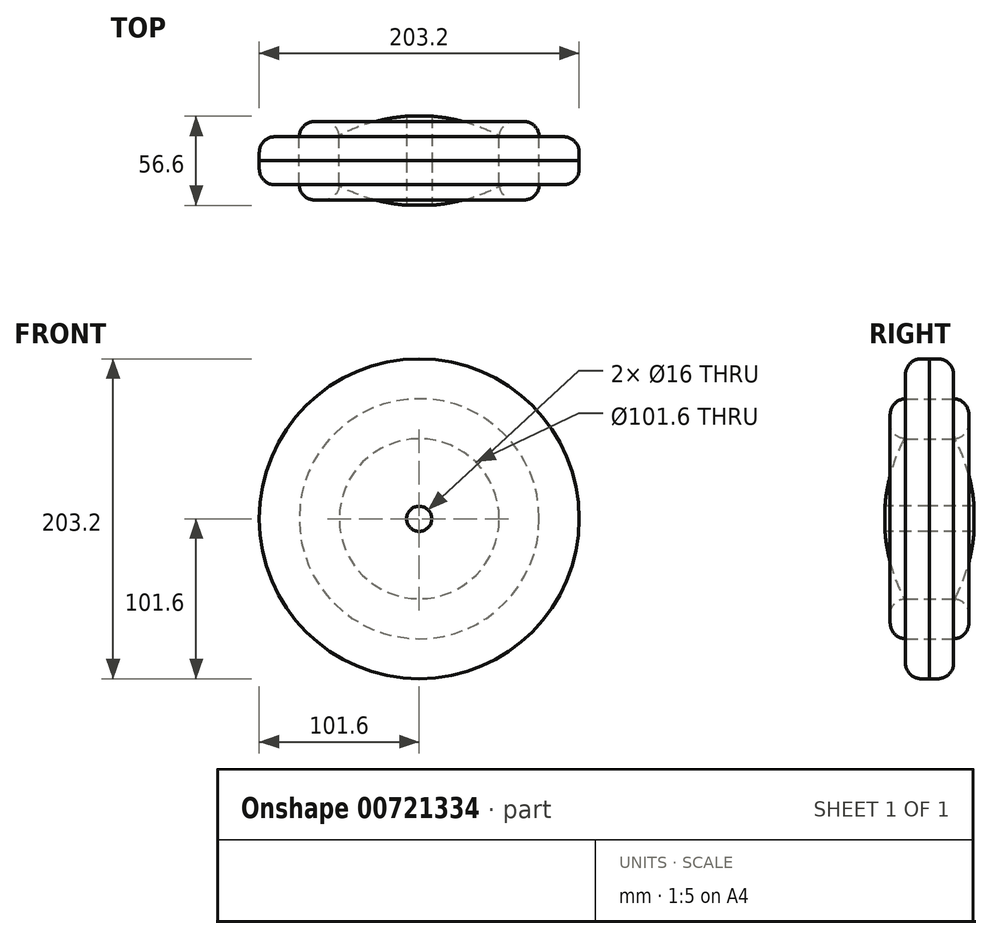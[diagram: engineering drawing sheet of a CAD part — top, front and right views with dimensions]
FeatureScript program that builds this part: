
annotation { "Feature Type Name" : "Feature", "Feature Type Description" : "" }
export const myFeature = defineFeature(function(context is Context, id is Id, definition is map)
    precondition{}
    {
        {
            var Q0;
            Q0=qCreatedBy(makeId("Front.planeOp"),FACE);
            var sketch = newSketch(context, id + "F0", { "sketchPlane" : qUnion([Q0])});
            skCircle(sketch, "E0", {"center": v(0, 0) * mm, "radius": 76.2 * mm});
            skCircle(sketch, "E1", {"center": v(0, 0) * mm, "radius": 50.8 * mm});
            skSolve(sketch);
        }
        {
            var Q0;
            Q0=makeQuery(id+"F0.imprint","IMPRINT",FACE,{"disambiguationData":[TD([[makeQuery(id+"F0.imprint","IMPRINT",EDGE,{"derivedFrom":sQuery(id+"F0.wireOp",EDGE,"E0")}),1.0]])]});
            extrude(context, id + "F1", {"entities" : qUnion([Q0]), "endBound" : BoundingType.SYMMETRIC, "depth" : 50 * mm, "offsetDistance" : 25 * mm});
        }
        {
            var Q0;
            Q0=makeQuery(id+"F1.opExtrude","CAP_EDGE",EDGE,{"disambiguationData":[OSD([sQuery(id+"F0.wireOp",EDGE,"E0")])],"isStart":false});
            var Q1;
            Q1=makeQuery(id+"F1.opExtrude","CAP_EDGE",EDGE,{"disambiguationData":[OSD([sQuery(id+"F0.wireOp",EDGE,"E0")])],"isStart":true});
            var Q2;
            Q2=makeQuery(id+"F1.opExtrude","CAP_EDGE",EDGE,{"disambiguationData":[OSD([sQuery(id+"F0.wireOp",EDGE,"E1")])],"isStart":false});
            var Q3;
            Q3=makeQuery(id+"F1.opExtrude","CAP_EDGE",EDGE,{"disambiguationData":[OSD([sQuery(id+"F0.wireOp",EDGE,"E1")])],"isStart":true});
            fillet(context, id + "F2", {"entities" : qUnion([Q0, Q1, Q2, Q3]), "radius" : 10 * mm, "tangentPropagation" : true, "allowEdgeOverflow" : false});
        }
        {
            var Q0;
            Q0=qCreatedBy(makeId("Right.planeOp"),FACE);
            var sketch = newSketch(context, id + "F3", { "sketchPlane" : qUnion([Q0])});
            skLineSegment(sketch, "E2", {"start": v(0, 0) * mm, "end": v(0, 101.6) * mm});
            skLineSegment(sketch, "E3", {"start": v(0, 101.6) * mm, "end": v(-5.28, 101.6) * mm});
            skLineSegment(sketch, "E4", {"start": v(-15.28, 91.6) * mm, "end": v(-15.28, 55.43) * mm});
            skLineSegment(sketch, "E5", {"start": v(0, 0) * mm, "end": v(-28.64, 0) * mm});
            skArc(sketch, "E6", {"start": v(-16.56, 50.04) * mm, "mid": v(-25.47, 25.72) * mm, "end": v(-28.64, 0) * mm});
            skPoint(sketch, "E7.visualSharp", {"position": v(-15.28, 52.5) * mm});
            skArc(sketch, "E7.filletArc", {"start": v(-16.56, 50.04) * mm, "mid": v(-15.6, 52.66) * mm, "end": v(-15.28, 55.43) * mm});
            skPoint(sketch, "E8.visualSharp", {"position": v(-15.28, 101.6) * mm});
            skArc(sketch, "E8.filletArc", {"start": v(-5.28, 101.6) * mm, "mid": v(-12.35, 98.67) * mm, "end": v(-15.28, 91.6) * mm});
            skSolve(sketch);
        }
        {
            var Q0;
            Q0 = qSketchRegion(id + "F3", true);
            var Q1;
            Q1=sQuery(id+"F3.wireOp",EDGE,"E5");
            revolve(context, id + "F4", {"surfaceOperationType" : NewSurfaceOperationType.NEW, "entities" : qUnion([Q0]), "axis" : qUnion([Q1]), "revolveType" : RevolveType.FULL});
        }
        {
            var Q0;
            Q0=makeQuery(id+"F4.opRevolve","SWEPT_BODY",BODY,{"disambiguationData":[OSD([sQuery(id+"F3.wireOp",EDGE,"E2"),sQuery(id+"F3.wireOp",EDGE,"E3"),sQuery(id+"F3.wireOp",EDGE,"E4"),sQuery(id+"F3.wireOp",EDGE,"E5"),sQuery(id+"F3.wireOp",EDGE,"E6"),sQuery(id+"F3.wireOp",EDGE,"E7.filletArc"),sQuery(id+"F3.wireOp",EDGE,"E8.filletArc")])]});
            var Q1;
            Q1=makeQuery(id+"F4.opRevolve","SWEPT_FACE",FACE,{"disambiguationData":[OSD([sQuery(id+"F3.wireOp",EDGE,"E2")])]});
            mirror(context, id + "F5", {"entities" : qUnion([Q0]), "mirrorPlane" : qUnion([Q1])});
        }
        {
            var Q0;
            Q0=qCreatedBy(makeId("Front.planeOp"),FACE);
            var sketch = newSketch(context, id + "F6", { "sketchPlane" : qUnion([Q0])});
            skCircle(sketch, "E9", {"center": v(0, 0) * mm, "radius": 8 * mm});
            skSolve(sketch);
        }
        {
            var Q0;
            Q0 = qSketchRegion(id + "F6", true);
            extrude(context, id + "F7", {"entities" : qUnion([Q0]), "operationType" : NewBodyOperationType.REMOVE, "endBound" : BoundingType.THROUGH_ALL, "oppositeDirection" : true, "depth" : 230 * mm, "offsetDistance" : 25 * mm, "hasSecondDirection" : true, "secondDirectionBound" : SecondDirectionBoundingType.THROUGH_ALL, "secondDirectionOppositeDirection" : false, "secondDirectionDepth" : 104 * mm});
        }
    });
